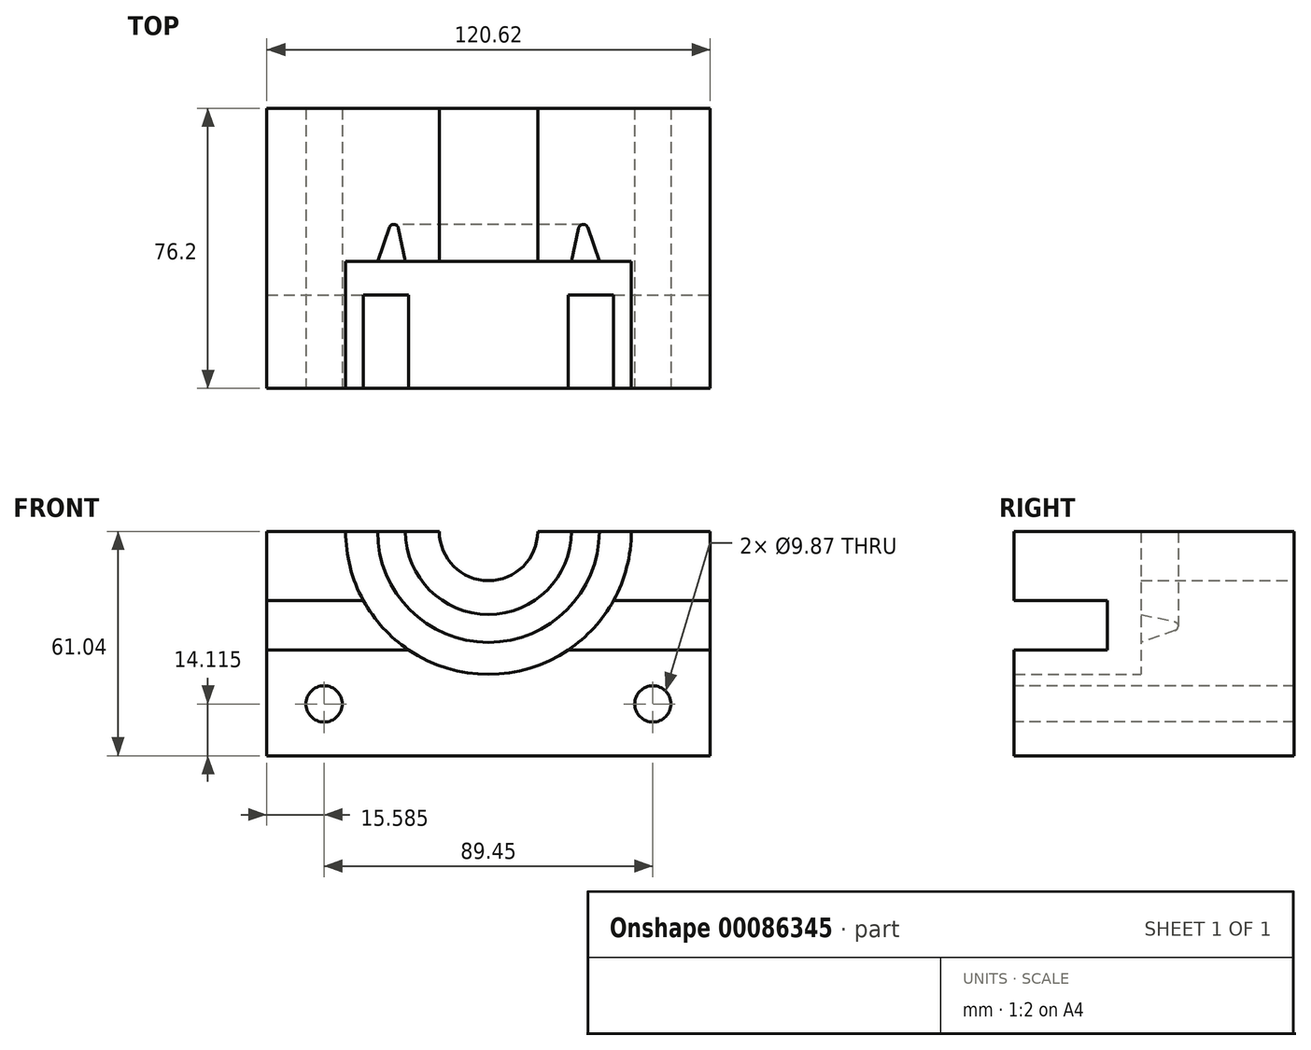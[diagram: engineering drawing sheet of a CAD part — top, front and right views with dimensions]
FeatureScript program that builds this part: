
annotation { "Feature Type Name" : "Feature", "Feature Type Description" : "" }
export const myFeature = defineFeature(function(context is Context, id is Id, definition is map)
    precondition{}
    {
        {
            var Q0;
            Q0=qCreatedBy(makeId("Front.planeOp"),FACE);
            var sketch = newSketch(context, id + "F0", { "sketchPlane" : qUnion([Q0])});
            skLineSegment(sketch, "E0.bottom", {"start": v(60.3, 30.52) * mm, "end": v(-60.3, 30.52) * mm});
            skLineSegment(sketch, "E0.top", {"start": v(60.3, -30.52) * mm, "end": v(-60.3, -30.52) * mm});
            skLineSegment(sketch, "E0.left", {"start": v(60.3, 30.52) * mm, "end": v(60.3, -30.52) * mm});
            skLineSegment(sketch, "E0.right", {"start": v(-60.3, 30.52) * mm, "end": v(-60.3, -30.52) * mm});
            skPoint(sketch, "E0.middle", {"position": v(0, 0) * mm});
            skSolve(sketch);
        }
        {
            var Q0;
            Q0 = qSketchRegion(id + "F0", true);
            extrude(context, id + "F1", {"entities" : qUnion([Q0]), "depth" : 76.2 * mm});
        }
        {
            var Q0;
            Q0=makeQuery(id+"F1.opExtrude","SWEPT_FACE",FACE,{"disambiguationData":[OSD([sQuery(id+"F0.wireOp",EDGE,"E0.bottom")])]});
            var sketch = newSketch(context, id + "F2", { "sketchPlane" : qUnion([Q0])});
            skLineSegment(sketch, "E1", {"start": v(0, 0) * mm, "end": v(-13.38, 0) * mm});
            skLineSegment(sketch, "E2", {"start": v(-13.38, 0) * mm, "end": v(-13.38, -41.68) * mm});
            skLineSegment(sketch, "E3", {"start": v(-13.38, -41.68) * mm, "end": v(-22.57, -41.68) * mm});
            skLineSegment(sketch, "E4", {"start": v(-22.57, -41.68) * mm, "end": v(-25.48, -28.14) * mm});
            skLineSegment(sketch, "E5", {"start": v(-25.48, -28.14) * mm, "end": v(-30.16, -41.68) * mm});
            skLineSegment(sketch, "E6", {"start": v(-30.16, -41.68) * mm, "end": v(-38.86, -41.68) * mm});
            skLineSegment(sketch, "E7", {"start": v(-38.86, -41.68) * mm, "end": v(-38.86, -76.2) * mm});
            skLineSegment(sketch, "E8", {"start": v(-38.86, -76.2) * mm, "end": v(0, -76.2) * mm});
            skLineSegment(sketch, "E9", {"start": v(0, -76.2) * mm, "end": v(0, 0) * mm});
            skLineSegment(sketch, "E10", {"start": v(0, 32.9) * mm, "end": v(0, -94.3) * mm, "construction": true});
            skSolve(sketch);
        }
        {
            var Q0;
            Q0 = qSketchRegion(id + "F2", true);
            var Q1;
            Q1=sQuery(id+"F2.wireOp",EDGE,"E10");
            var Q2;
            Q2=sQuery(id+"F2.wireOp",EDGE,"E10");
            revolve(context, id + "F3", {"operationType" : NewBodyOperationType.REMOVE, "entities" : qUnion([Q0]), "surfaceEntities" : qUnion([Q1]), "axis" : qUnion([Q2]), "revolveType" : RevolveType.ONE_DIRECTION, "angle" : 180 * degree});
        }
        {
            var Q0;
            Q0=makeQuery(id+"F1.opExtrude","CAP_FACE",FACE,{"disambiguationData":[OSD([sQuery(id+"F0.wireOp",EDGE,"E0.bottom"),sQuery(id+"F0.wireOp",EDGE,"E0.top"),sQuery(id+"F0.wireOp",EDGE,"E0.left"),sQuery(id+"F0.wireOp",EDGE,"E0.right")])],"isStart":false});
            var sketch = newSketch(context, id + "F4", { "sketchPlane" : qUnion([Q0])});
            skLineSegment(sketch, "E11.bottom", {"start": v(-60.3, 11.75) * mm, "end": v(60.3, 11.75) * mm});
            skLineSegment(sketch, "E11.top", {"start": v(-60.3, -1.7) * mm, "end": v(60.3, -1.7) * mm});
            skLineSegment(sketch, "E11.left", {"start": v(-60.3, 11.75) * mm, "end": v(-60.3, -1.7) * mm});
            skLineSegment(sketch, "E11.right", {"start": v(60.3, 11.75) * mm, "end": v(60.3, -1.7) * mm});
            skSolve(sketch);
        }
        {
            var Q0;
            Q0 = qSketchRegion(id + "F4", true);
            extrude(context, id + "F5", {"entities" : qUnion([Q0]), "operationType" : NewBodyOperationType.REMOVE, "oppositeDirection" : true, "depth" : 25.4 * mm});
        }
        {
            var Q0;
            Q0=makeQuery(id+"F3.boolean.opBoolean","COPY",EDGE,{"derivedFrom":makeQuery(id+"F3.opRevolve","SWEPT_EDGE",EDGE,{"disambiguationData":[OSD([sQuery(id+"F2.wireOp",EDGE,"E4"),sQuery(id+"F2.wireOp",EDGE,"E5")])]})});
            fillet(context, id + "F6", {"entities" : qUnion([Q0]), "radius" : 1.27 * mm, "tangentPropagation" : true, "allowEdgeOverflow" : false});
        }
        {
            var Q0;
            {var subQ0=sQuery(id+"F0.wireOp",EDGE,"E0.right");var subQ1=sQuery(id+"F0.wireOp",EDGE,"E0.left");var subQ2=sQuery(id+"F0.wireOp",EDGE,"E0.top");Q0=makeQuery(id+"F5.boolean.opBoolean","SPLIT",FACE,{"disambiguationData":[TD([makeQuery(id+"F1.opExtrude","SWEPT_FACE",FACE,{"disambiguationData":[OSD([subQ2])]}),makeQuery(id+"F1.opExtrude","SWEPT_FACE",FACE,{"disambiguationData":[OSD([subQ1])]}),makeQuery(id+"F1.opExtrude","SWEPT_FACE",FACE,{"disambiguationData":[OSD([subQ0])]}),makeQuery(id+"F3.boolean.opBoolean","COPY",FACE,{"derivedFrom":makeQuery(id+"F3.opRevolve","SWEPT_FACE",FACE,{"disambiguationData":[OSD([sQuery(id+"F2.wireOp",EDGE,"E7")])]})}),makeQuery(id+"F5.opExtrude","SWEPT_FACE",FACE,{"disambiguationData":[OSD([sQuery(id+"F4.wireOp",EDGE,"E11.top")])]})])],"derivedFrom":makeQuery(id+"F1.opExtrude","CAP_FACE",FACE,{"disambiguationData":[OSD([sQuery(id+"F0.wireOp",EDGE,"E0.bottom"),subQ2,subQ1,subQ0])],"isStart":false})});}
            var sketch = newSketch(context, id + "F7", { "sketchPlane" : qUnion([Q0])});
            skCircle(sketch, "E12", {"center": v(-44.72, -16.4) * mm, "radius": 4.94 * mm});
            skCircle(sketch, "E13.MirrorC", {"center": v(44.72, -16.4) * mm, "radius": 4.94 * mm});
            skSolve(sketch);
        }
        {
            var Q0;
            Q0 = qSketchRegion(id + "F7", true);
            extrude(context, id + "F8", {"entities" : qUnion([Q0]), "operationType" : NewBodyOperationType.REMOVE, "oppositeDirection" : true, "depth" : 76.2 * mm});
        }
    });
